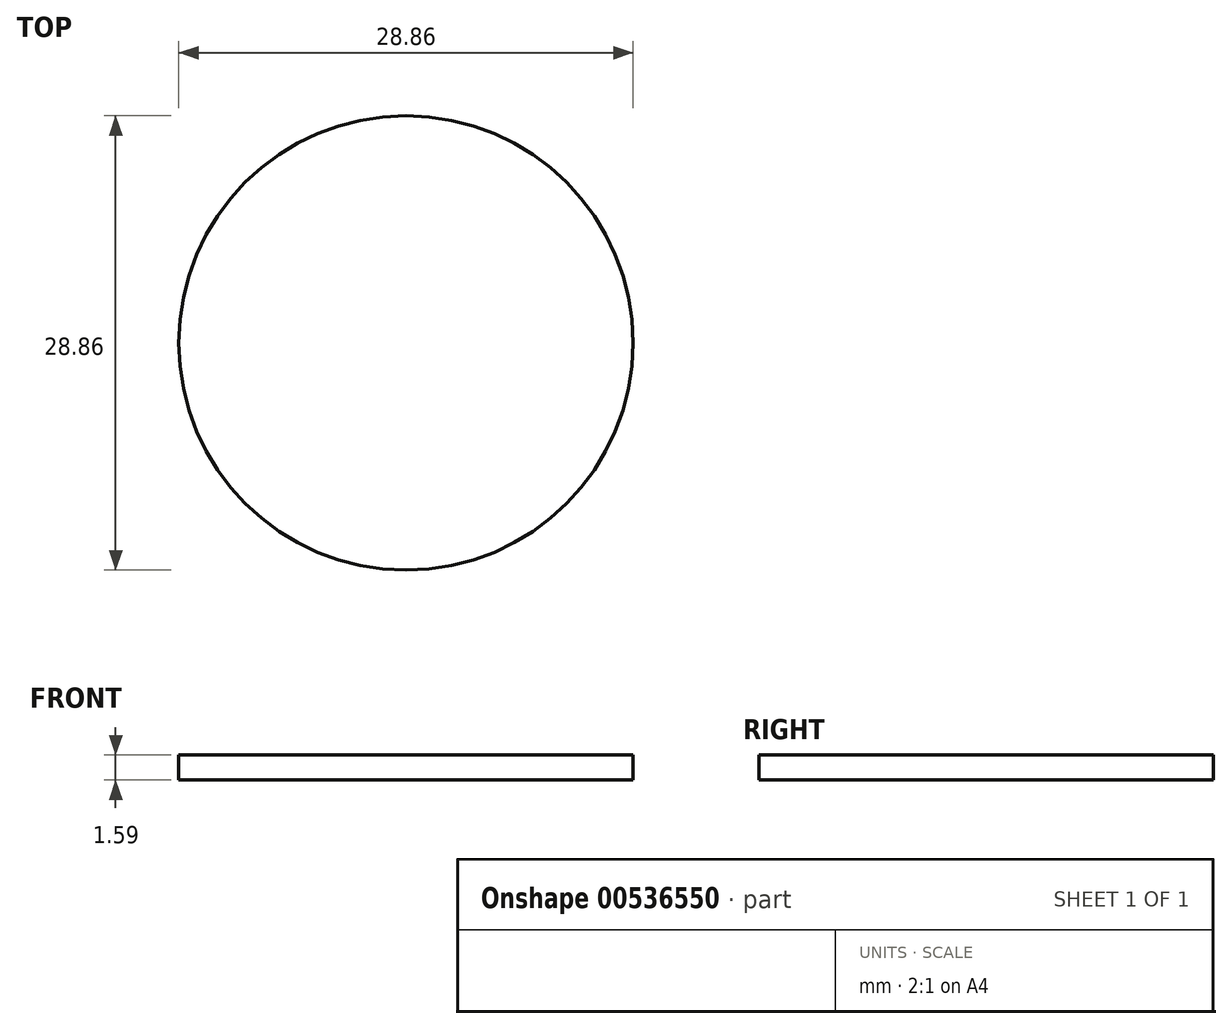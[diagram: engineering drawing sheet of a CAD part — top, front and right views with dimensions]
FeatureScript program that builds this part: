
annotation { "Feature Type Name" : "Feature", "Feature Type Description" : "" }
export const myFeature = defineFeature(function(context is Context, id is Id, definition is map)
    precondition{}
    {
        {
            var Q0;
            Q0=qCreatedBy(makeId("Top.planeOp"),FACE);
            var sketch = newSketch(context, id + "F0", { "sketchPlane" : qUnion([Q0])});
            skCircle(sketch, "E0", {"center": v(0, 0) * mm, "radius": 14.43 * mm});
            skSolve(sketch);
        }
        {
            var Q0;
            Q0 = qSketchRegion(id + "F0", true);
            extrude(context, id + "F1", {"entities" : qUnion([Q0]), "depth" : 1.59 * mm, "offsetDistance" : 25.4 * mm});
        }
    });
